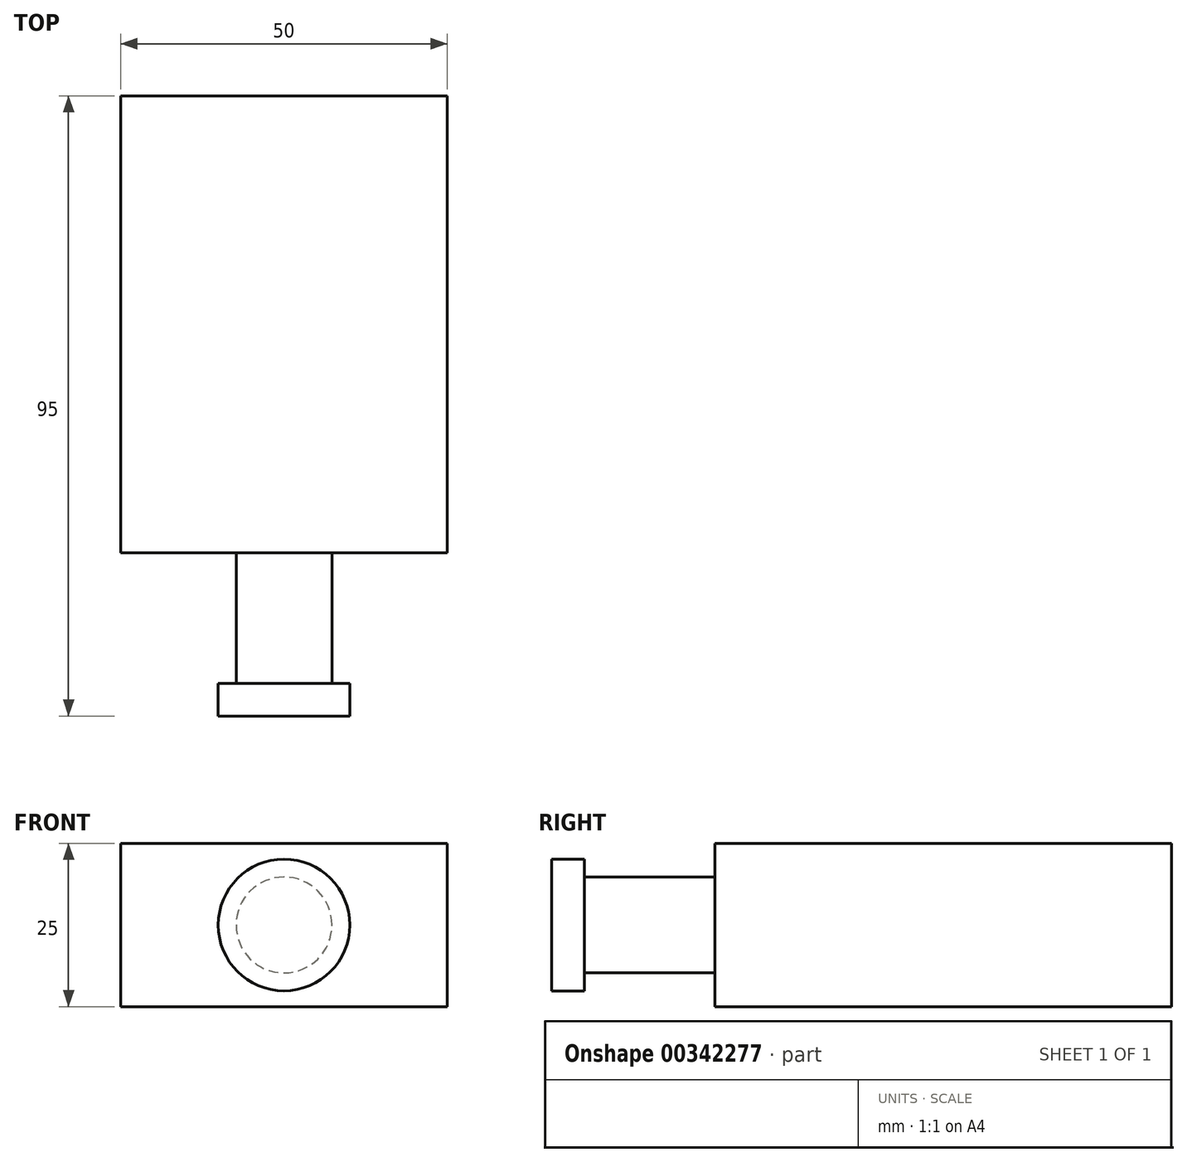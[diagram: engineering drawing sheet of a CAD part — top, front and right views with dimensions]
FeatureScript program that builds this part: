
annotation { "Feature Type Name" : "Feature", "Feature Type Description" : "" }
export const myFeature = defineFeature(function(context is Context, id is Id, definition is map)
    precondition{}
    {
        {
            var Q0;
            Q0=qCreatedBy(makeId("Front.planeOp"),FACE);
            var sketch = newSketch(context, id + "F0", { "sketchPlane" : qUnion([Q0])});
            skPoint(sketch, "E0.middle", {"position": v(0, 0) * mm});
            skLineSegment(sketch, "E1.bottom", {"start": v(-25, 12.5) * mm, "end": v(25, 12.5) * mm});
            skLineSegment(sketch, "E1.top", {"start": v(-25, -12.5) * mm, "end": v(25, -12.5) * mm});
            skLineSegment(sketch, "E1.left", {"start": v(-25, 12.5) * mm, "end": v(-25, -12.5) * mm});
            skLineSegment(sketch, "E1.right", {"start": v(25, 12.5) * mm, "end": v(25, -12.5) * mm});
            skSolve(sketch);
        }
        {
            var Q0;
            Q0=makeQuery(id+"F0.imprint","IMPRINT",FACE,{"disambiguationData":[TD([[makeQuery(id+"F0.imprint","IMPRINT",EDGE,{"derivedFrom":sQuery(id+"F0.wireOp",EDGE,"E1.bottom")}),-1.0]])]});
            extrude(context, id + "F1", {"entities" : qUnion([Q0]), "oppositeDirection" : true, "depth" : 70 * mm});
        }
        {
            var Q0;
            Q0=qCreatedBy(makeId("Front.planeOp"),FACE);
            var sketch = newSketch(context, id + "F2", { "sketchPlane" : qUnion([Q0])});
            skCircle(sketch, "E2", {"center": v(0, 0) * mm, "radius": 7.34 * mm});
            skSolve(sketch);
        }
        {
            var Q0;
            Q0=makeQuery(id+"F2.imprint","IMPRINT",FACE,{"disambiguationData":[TD([[makeQuery(id+"F2.imprint","IMPRINT",EDGE,{"derivedFrom":sQuery(id+"F2.wireOp",EDGE,"E2")}),1.0]])]});
            extrude(context, id + "F3", {"entities" : qUnion([Q0]), "operationType" : NewBodyOperationType.ADD, "depth" : 20 * mm});
        }
        {
            var Q0;
            Q0=makeQuery(id+"F3.opExtrude","CAP_FACE",FACE,{"disambiguationData":[OSD([sQuery(id+"F2.wireOp",EDGE,"E2")])],"isStart":false});
            var sketch = newSketch(context, id + "F4", { "sketchPlane" : qUnion([Q0])});
            skCircle(sketch, "E3", {"center": v(0, 0) * mm, "radius": 10.08 * mm});
            skSolve(sketch);
        }
        {
            var Q0;
            Q0=makeQuery(id+"F4.imprint","IMPRINT",FACE,{"disambiguationData":[TD([[makeQuery(id+"F4.imprint","IMPRINT",EDGE,{"derivedFrom":makeQuery(id+"F3.opExtrude","CAP_EDGE",EDGE,{"disambiguationData":[OSD([sQuery(id+"F2.wireOp",EDGE,"E2")])],"isStart":false})}),1.0]])]});
            var Q1;
            Q1=makeQuery(id+"F4.imprint","IMPRINT",FACE,{"disambiguationData":[TD([[makeQuery(id+"F4.imprint","IMPRINT",EDGE,{"derivedFrom":sQuery(id+"F4.wireOp",EDGE,"E3")}),1.0]])]});
            extrude(context, id + "F5", {"entities" : qUnion([Q0, Q1]), "operationType" : NewBodyOperationType.ADD, "depth" : 5 * mm});
        }
    });
